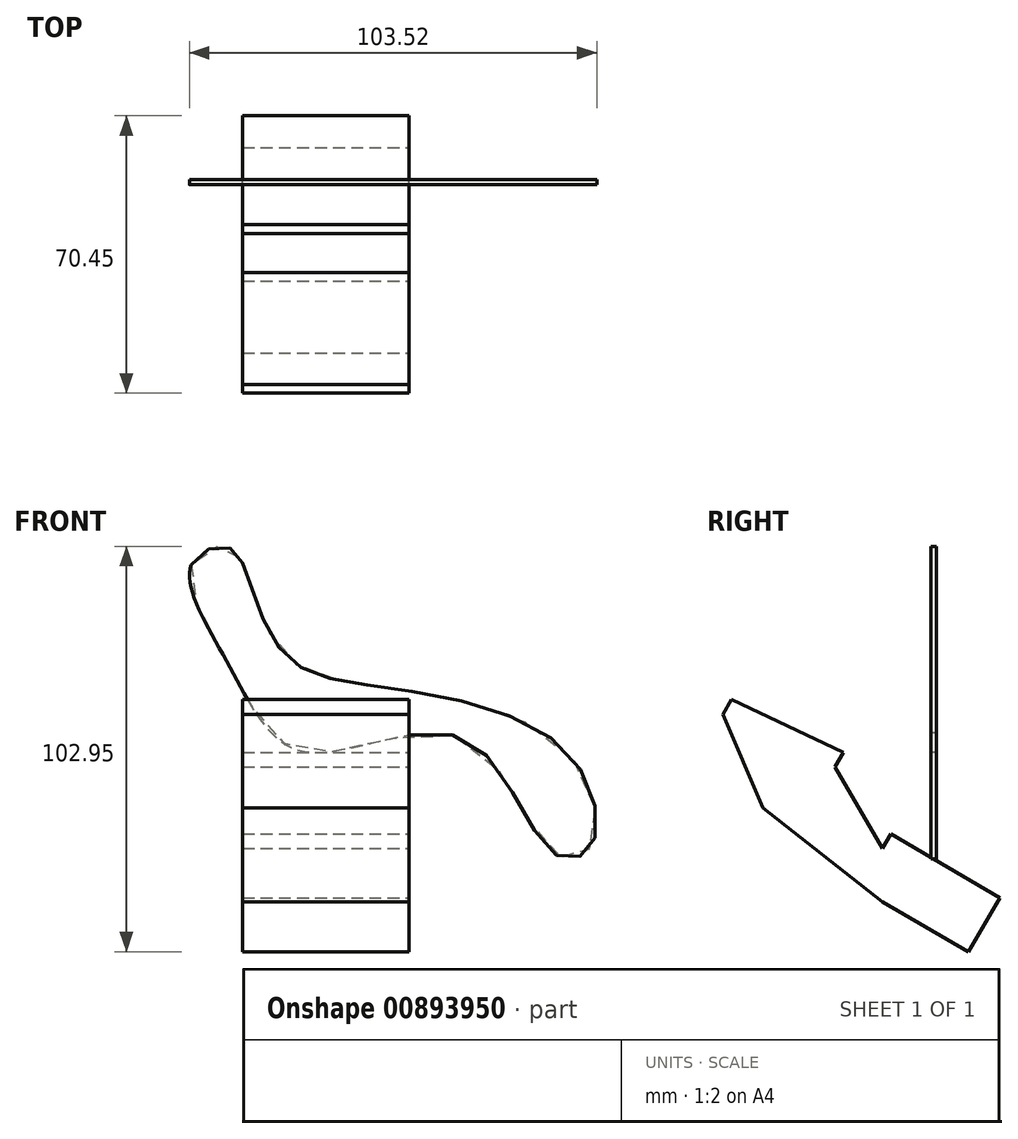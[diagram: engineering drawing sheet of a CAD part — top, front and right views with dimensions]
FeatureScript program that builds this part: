
annotation { "Feature Type Name" : "Feature", "Feature Type Description" : "" }
export const myFeature = defineFeature(function(context is Context, id is Id, definition is map)
    precondition{}
    {
        {
            var Q0;
            Q0=qCreatedBy(makeId("Front.planeOp"),FACE);
            var sketch = newSketch(context, id + "F0", { "sketchPlane" : qUnion([Q0])});
            skFitSpline(sketch, "E0", {"points": [v(-55.36, 66.3) * mm, v(-45.68, 40.58) * mm, v(-26.42, 18.86) * mm, v(14, 22.07) * mm, v(36.47, -6.83) * mm, v(46.27, -5.12) * mm, v(39.44, 19.45) * mm, v(-7.33, 35.26) * mm, v(-31.03, 42.9) * mm, v(-40.66, 62.36) * mm, v(-46.2, 70.75) * mm, v(-55.36, 66.3) * mm]});
            skSolve(sketch);
        }
        {
            var Q0;
            Q0 = qSketchRegion(id + "F0", true);
            extrude(context, id + "F1", {"entities" : qUnion([Q0]), "oppositeDirection" : true, "depth" : 1.3 * mm, "offsetDistance" : 25 * mm});
        }
        {
            var Q0;
            Q0=qCreatedBy(makeId("Right.planeOp"),FACE);
            var sketch = newSketch(context, id + "F2", { "sketchPlane" : qUnion([Q0])});
            skLineSegment(sketch, "E1", {"start": v(-52.92, 28.34) * mm, "end": v(-42.78, 4.56) * mm});
            skLineSegment(sketch, "E2", {"start": v(-42.78, 4.56) * mm, "end": v(-12.34, -19.33) * mm});
            skLineSegment(sketch, "E3", {"start": v(-52.92, 28.34) * mm, "end": v(-24.48, 14.9) * mm});
            skLineSegment(sketch, "E4", {"start": v(-24.48, 14.9) * mm, "end": v(-12.34, -5.73) * mm});
            skLineSegment(sketch, "E5", {"start": v(-12.34, -5.73) * mm, "end": v(15.36, -21.97) * mm});
            skLineSegment(sketch, "E6", {"start": v(15.36, -21.97) * mm, "end": v(9.47, -32.01) * mm});
            skLineSegment(sketch, "E7", {"start": v(9.47, -32.01) * mm, "end": v(-12.34, -19.33) * mm});
            skSolve(sketch);
        }
        {
            var Q0;
            Q0 = qSketchRegion(id + "F2", true);
            extrude(context, id + "F3", {"entities" : qUnion([Q0]), "oppositeDirection" : true, "depth" : 42.3 * mm, "offsetDistance" : 25 * mm});
        }
        {
            var Q0;
            Q0=makeQuery(id+"F3.opExtrude","SWEPT_FACE",FACE,{"disambiguationData":[OSD([sQuery(id+"F2.wireOp",EDGE,"E5")])]});
            var Q1;
            Q1=makeQuery(id+"F3.opExtrude","SWEPT_FACE",FACE,{"disambiguationData":[OSD([sQuery(id+"F2.wireOp",EDGE,"E3")])]});
            extrude(context, id + "F4", {"entities" : qUnion([Q0, Q1]), "operationType" : NewBodyOperationType.ADD, "depth" : 4.3 * mm, "offsetDistance" : 25 * mm});
        }
    });
